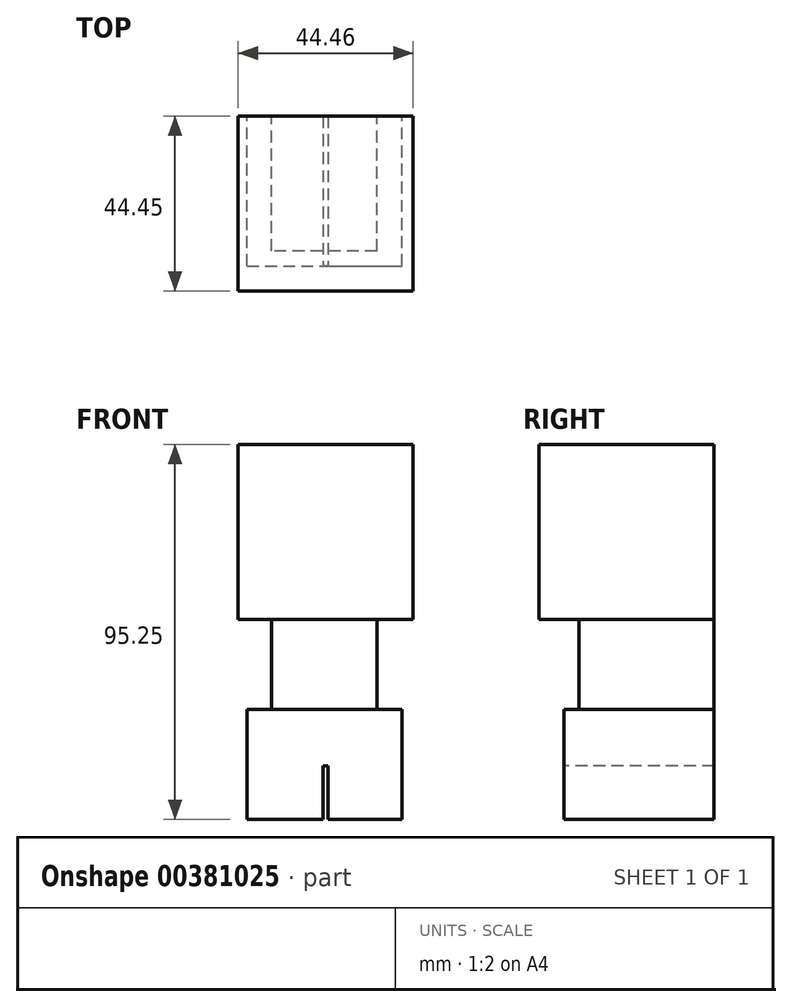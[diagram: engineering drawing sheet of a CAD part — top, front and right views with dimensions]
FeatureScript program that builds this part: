
annotation { "Feature Type Name" : "Feature", "Feature Type Description" : "" }
export const myFeature = defineFeature(function(context is Context, id is Id, definition is map)
    precondition{}
    {
        {
            var Q0;
            Q0=qCreatedBy(makeId("Front.planeOp"),FACE);
            var sketch = newSketch(context, id + "F0", { "sketchPlane" : qUnion([Q0])});
            skLineSegment(sketch, "E0.bottom", {"start": v(-22.23, 95.25) * mm, "end": v(22.22, 95.25) * mm});
            skLineSegment(sketch, "E0.top", {"start": v(-22.23, 50.8) * mm, "end": v(22.23, 50.8) * mm});
            skLineSegment(sketch, "E0.left", {"start": v(-22.23, 95.25) * mm, "end": v(-22.23, 50.8) * mm});
            skLineSegment(sketch, "E0.right", {"start": v(22.22, 95.25) * mm, "end": v(22.22, 50.8) * mm});
            skPoint(sketch, "E1", {"position": v(0, 50.8) * mm});
            skSolve(sketch);
        }
        {
            var Q0;
            Q0 = qSketchRegion(id + "F0", true);
            extrude(context, id + "F1", {"entities" : qUnion([Q0]), "depth" : 44.45 * mm});
        }
        {
            var Q0;
            Q0=qCreatedBy(makeId("Front.planeOp"),FACE);
            var sketch = newSketch(context, id + "F2", { "sketchPlane" : qUnion([Q0])});
            skLineSegment(sketch, "E2", {"start": v(-10.87, 51.04) * mm, "end": v(-10.87, 27.9) * mm});
            skLineSegment(sketch, "E3", {"start": v(-10.87, 27.9) * mm, "end": v(10.25, 27.9) * mm});
            skLineSegment(sketch, "E4", {"start": v(10.25, 51.04) * mm, "end": v(10.25, 27.9) * mm});
            skLineSegment(sketch, "E5", {"start": v(-19.96, 0) * mm, "end": v(19.34, 0) * mm});
            skLineSegment(sketch, "E6", {"start": v(0, 0) * mm, "end": v(0, 5.58) * mm});
            skLineSegment(sketch, "E7", {"start": v(75.52, 99) * mm, "end": v(77.27, 82.9) * mm});
            skLineSegment(sketch, "E8", {"start": v(75.52, 99) * mm, "end": v(82.21, 99) * mm});
            skLineSegment(sketch, "E9", {"start": v(86.84, 97.25) * mm, "end": v(88.4, 82.9) * mm});
            skLineSegment(sketch, "E10", {"start": v(88.4, 82.9) * mm, "end": v(77.27, 82.9) * mm});
            skLineSegment(sketch, "E11", {"start": v(-10.87, 27.9) * mm, "end": v(-19.96, 27.9) * mm});
            skLineSegment(sketch, "E12", {"start": v(-19.96, 27.9) * mm, "end": v(-19.96, 0) * mm});
            skLineSegment(sketch, "E13", {"start": v(10.25, 27.9) * mm, "end": v(19.34, 27.9) * mm});
            skLineSegment(sketch, "E14", {"start": v(19.34, 27.9) * mm, "end": v(19.34, 0) * mm});
            skSolve(sketch);
        }
        {
            var Q0;
            Q0 = qSketchRegion(id + "F2", true);
            extrude(context, id + "F3", {"entities" : qUnion([Q0]), "depth" : 38.1 * mm});
        }
        {
            var Q0;
            Q0=qCreatedBy(makeId("Front.planeOp"),FACE);
            var sketch = newSketch(context, id + "F4", { "sketchPlane" : qUnion([Q0])});
            skLineSegment(sketch, "E15", {"start": v(-13.7, 27.9) * mm, "end": v(-13.7, 50.8) * mm});
            skLineSegment(sketch, "E16", {"start": v(13, 27.9) * mm, "end": v(13, 50.8) * mm});
            skLineSegment(sketch, "E17", {"start": v(-13.7, 50.8) * mm, "end": v(-13.7, 27.9) * mm});
            skLineSegment(sketch, "E18", {"start": v(-13.7, 50.8) * mm, "end": v(13, 50.8) * mm});
            skLineSegment(sketch, "E19", {"start": v(13, 27.9) * mm, "end": v(-13.7, 27.9) * mm});
            skSolve(sketch);
        }
        {
            var Q0;
            Q0 = qSketchRegion(id + "F4", true);
            extrude(context, id + "F5", {"entities" : qUnion([Q0]), "operationType" : NewBodyOperationType.ADD, "depth" : 34.3 * mm});
        }
        {
            var Q0;
            Q0=makeQuery(id+"F3.opExtrude","CAP_FACE",FACE,{"disambiguationData":[OSD([sQuery(id+"F2.wireOp",EDGE,"E3"),sQuery(id+"F2.wireOp",EDGE,"E5"),sQuery(id+"F2.wireOp",EDGE,"E11"),sQuery(id+"F2.wireOp",EDGE,"E12"),sQuery(id+"F2.wireOp",EDGE,"E13"),sQuery(id+"F2.wireOp",EDGE,"E14")])],"isStart":false});
            var sketch = newSketch(context, id + "F6", { "sketchPlane" : qUnion([Q0])});
            skLineSegment(sketch, "E20.bottom", {"start": v(0.64, 13.6) * mm, "end": v(-0.64, 13.6) * mm});
            skLineSegment(sketch, "E20.top", {"start": v(0.64, -0.4) * mm, "end": v(-0.64, -0.4) * mm});
            skLineSegment(sketch, "E20.left", {"start": v(0.64, 13.6) * mm, "end": v(0.64, -0.4) * mm});
            skLineSegment(sketch, "E20.right", {"start": v(-0.64, 13.6) * mm, "end": v(-0.64, -0.4) * mm});
            skPoint(sketch, "E20.middle", {"position": v(0, 6.6) * mm});
            skSolve(sketch);
        }
        {
            var Q0;
            Q0 = qSketchRegion(id + "F6", true);
            extrude(context, id + "F7", {"entities" : qUnion([Q0]), "operationType" : NewBodyOperationType.REMOVE, "oppositeDirection" : true, "depth" : 42.93 * mm});
        }
    });
